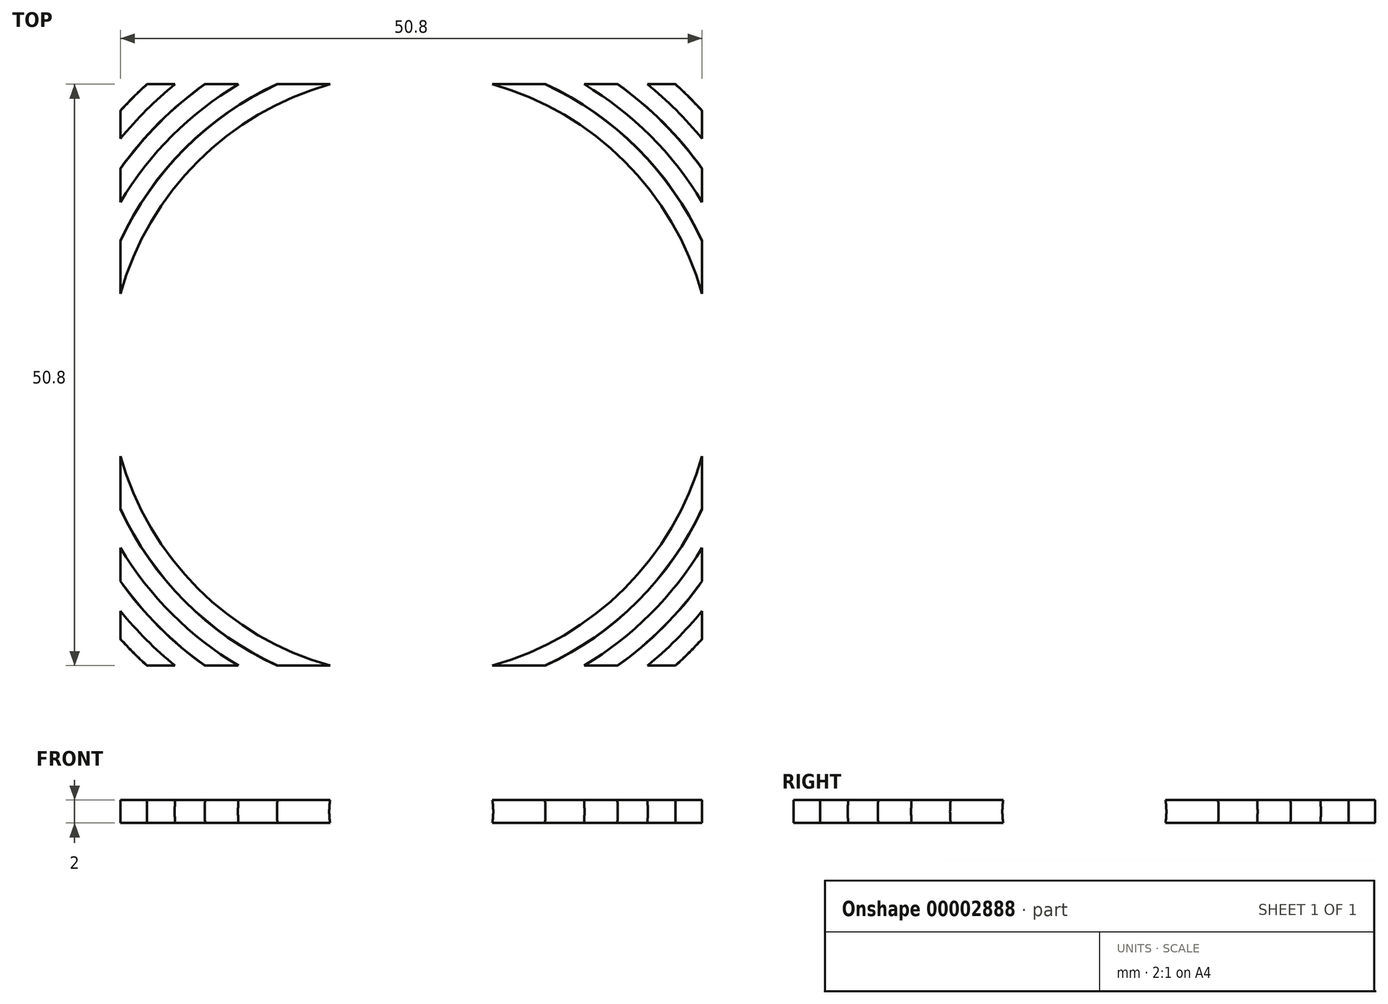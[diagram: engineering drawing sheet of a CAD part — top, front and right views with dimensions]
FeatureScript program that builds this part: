
annotation { "Feature Type Name" : "Feature", "Feature Type Description" : "" }
export const myFeature = defineFeature(function(context is Context, id is Id, definition is map)
    precondition{}
    {
        {
            assignVariable(context, id + "F0", {"name" : "CubeWidth", "anyValue" : 2});
        }
        {
            var Q0;
            Q0=qCreatedBy(makeId("Top.planeOp"),FACE);
            var sketch = newSketch(context, id + "F1", { "sketchPlane" : qUnion([Q0])});
            skArc(sketch, "E0", {"start": v(0, 31.15) * mm, "mid": v(-31.15, 0) * mm, "end": v(0, -31.15) * mm});
            skArc(sketch, "E1", {"start": v(0, 32.74) * mm, "mid": v(-32.74, 0) * mm, "end": v(0, -32.74) * mm});
            skArc(sketch, "E2", {"start": v(0, 35.92) * mm, "mid": v(-35.92, 0) * mm, "end": v(0, -35.92) * mm});
            skArc(sketch, "E3", {"start": v(0, 27.98) * mm, "mid": v(-27.98, 0) * mm, "end": v(0, -27.98) * mm});
            skArc(sketch, "E4", {"start": v(0, 29.57) * mm, "mid": v(-29.57, 0) * mm, "end": v(0, -29.57) * mm});
            skArc(sketch, "E5", {"start": v(0, 37.5) * mm, "mid": v(-37.5, 0) * mm, "end": v(0, -37.5) * mm});
            skArc(sketch, "E6", {"start": v(0, 34.33) * mm, "mid": v(-34.33, 0) * mm, "end": v(0, -34.33) * mm});
            skArc(sketch, "E7", {"start": v(0, 26.4) * mm, "mid": v(-26.4, 0) * mm, "end": v(0, -26.4) * mm});
            skLineSegment(sketch, "E8", {"start": v(0, 75.66) * mm, "end": v(0, -76.08) * mm});
            skSolve(sketch);
        }
        {
            var Q0;
            {var subQ0=sQuery(id+"F1.wireOp",EDGE,"E3");Q0=makeQuery(id+"F1.imprint","IMPRINT",FACE,{"disambiguationData":[TD([[makeQuery(id+"F1.imprint","IMPRINT",EDGE,{"derivedFrom":subQ0}),1.0]])]});}
            var Q1;
            {var subQ0=sQuery(id+"F1.wireOp",EDGE,"E0");Q1=makeQuery(id+"F1.imprint","IMPRINT",FACE,{"disambiguationData":[TD([[makeQuery(id+"F1.imprint","IMPRINT",EDGE,{"derivedFrom":subQ0}),1.0]])]});}
            var Q2;
            {var subQ0=sQuery(id+"F1.wireOp",EDGE,"E1");Q2=makeQuery(id+"F1.imprint","IMPRINT",FACE,{"disambiguationData":[TD([[makeQuery(id+"F1.imprint","IMPRINT",EDGE,{"derivedFrom":subQ0}),-1.0]])]});}
            var Q3;
            Q3=sQuery(id+"F1.wireOp",EDGE,"E8");
            revolve(context, id + "F2", {"surfaceOperationType" : NewSurfaceOperationType.NEW, "entities" : qUnion([Q0, Q1, Q2]), "axis" : qUnion([Q3]), "revolveType" : RevolveType.FULL});
        }
        {
            var Q0;
            Q0=qCreatedBy(makeId("Top.planeOp"),FACE);
            var sketch = newSketch(context, id + "F3", { "sketchPlane" : qUnion([Q0])});
            skLineSegment(sketch, "E9.bottom", {"start": v(25.4, -25.4) * mm, "end": v(-25.4, -25.4) * mm});
            skLineSegment(sketch, "E9.top", {"start": v(25.4, 25.4) * mm, "end": v(-25.4, 25.4) * mm});
            skLineSegment(sketch, "E9.left", {"start": v(25.4, -25.4) * mm, "end": v(25.4, 25.4) * mm});
            skLineSegment(sketch, "E9.right", {"start": v(-25.4, -25.4) * mm, "end": v(-25.4, 25.4) * mm});
            skPoint(sketch, "E9.middle", {"position": v(0, 0) * mm});
            skSolve(sketch);
        }
        {
            var Q0;
            Q0 = qSketchRegion(id + "F3", true);
            extrude(context, id + "F4", {"entities" : qUnion([Q0]), "depth" : (getVariable(context, 'CubeWidth') / 2) * mm, "offsetDistance" : 25.4 * mm, "hasSecondDirection" : true, "secondDirectionOppositeDirection" : true, "secondDirectionDepth" : (getVariable(context, 'CubeWidth') / 2) * mm});
        }
        {
            var Q0;
            Q0=makeQuery(id+"F4.opExtrude","SWEPT_BODY",BODY,{"disambiguationData":[OSD([sQuery(id+"F3.wireOp",EDGE,"E9.bottom"),sQuery(id+"F3.wireOp",EDGE,"E9.top"),sQuery(id+"F3.wireOp",EDGE,"E9.left"),sQuery(id+"F3.wireOp",EDGE,"E9.right")])]});
            var Q1;
            Q1=makeQuery(id+"F2.opRevolve","SWEPT_BODY",BODY,{"disambiguationData":[OSD([sQuery(id+"F1.wireOp",EDGE,"E0"),sQuery(id+"F1.wireOp",EDGE,"E4"),sQuery(id+"F1.wireOp",EDGE,"E8")])]});
            booleanBodies(context, id + "F5", {"operationType" : BooleanOperationType.INTERSECTION, "tools" : qUnion([Q0, Q1]), "keepTools" : true});
        }
        {
            var Q0;
            Q0=makeQuery(id+"F4.opExtrude","SWEPT_BODY",BODY,{"disambiguationData":[OSD([sQuery(id+"F3.wireOp",EDGE,"E9.bottom"),sQuery(id+"F3.wireOp",EDGE,"E9.top"),sQuery(id+"F3.wireOp",EDGE,"E9.left"),sQuery(id+"F3.wireOp",EDGE,"E9.right")])]});
            var Q1;
            Q1=makeQuery(id+"F2.opRevolve","SWEPT_BODY",BODY,{"disambiguationData":[OSD([sQuery(id+"F1.wireOp",EDGE,"E1"),sQuery(id+"F1.wireOp",EDGE,"E6"),sQuery(id+"F1.wireOp",EDGE,"E8")])]});
            booleanBodies(context, id + "F6", {"operationType" : BooleanOperationType.INTERSECTION, "tools" : qUnion([Q0, Q1]), "keepTools" : true});
        }
        {
            var Q0;
            Q0=makeQuery(id+"F2.opRevolve","SWEPT_BODY",BODY,{"disambiguationData":[OSD([sQuery(id+"F1.wireOp",EDGE,"E3"),sQuery(id+"F1.wireOp",EDGE,"E7"),sQuery(id+"F1.wireOp",EDGE,"E8")])]});
            var Q1;
            Q1=makeQuery(id+"F4.opExtrude","SWEPT_BODY",BODY,{"disambiguationData":[OSD([sQuery(id+"F3.wireOp",EDGE,"E9.bottom"),sQuery(id+"F3.wireOp",EDGE,"E9.top"),sQuery(id+"F3.wireOp",EDGE,"E9.left"),sQuery(id+"F3.wireOp",EDGE,"E9.right")])]});
            booleanBodies(context, id + "F7", {"operationType" : BooleanOperationType.INTERSECTION, "tools" : qUnion([Q0, Q1]), "keepTools" : true});
        }
        {
            var Q0;
            Q0=makeQuery(id+"F2.opRevolve","SWEPT_BODY",BODY,{"disambiguationData":[OSD([sQuery(id+"F1.wireOp",EDGE,"E1"),sQuery(id+"F1.wireOp",EDGE,"E6"),sQuery(id+"F1.wireOp",EDGE,"E8")])]});
            var Q1;
            Q1=makeQuery(id+"F2.opRevolve","SWEPT_BODY",BODY,{"disambiguationData":[OSD([sQuery(id+"F1.wireOp",EDGE,"E3"),sQuery(id+"F1.wireOp",EDGE,"E7"),sQuery(id+"F1.wireOp",EDGE,"E8")])]});
            var Q2;
            Q2=makeQuery(id+"F4.opExtrude","SWEPT_BODY",BODY,{"disambiguationData":[OSD([sQuery(id+"F3.wireOp",EDGE,"E9.bottom"),sQuery(id+"F3.wireOp",EDGE,"E9.top"),sQuery(id+"F3.wireOp",EDGE,"E9.left"),sQuery(id+"F3.wireOp",EDGE,"E9.right")])]});
            var Q3;
            Q3=makeQuery(id+"F2.opRevolve","SWEPT_BODY",BODY,{"disambiguationData":[OSD([sQuery(id+"F1.wireOp",EDGE,"E0"),sQuery(id+"F1.wireOp",EDGE,"E4"),sQuery(id+"F1.wireOp",EDGE,"E8")])]});
            deleteBodies(context, id + "F8", {"entities" : qUnion([Q0, Q1, Q2, Q3])});
        }
    });
